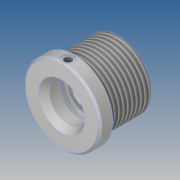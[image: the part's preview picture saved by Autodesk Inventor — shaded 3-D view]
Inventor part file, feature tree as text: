
AUTODESK INVENTOR PART (.ipt)
format: ipt  version: 2019 (Build 230136000, 136)  size: 200,704 bytes
history: native  units: mm
features: other x3, sketch x3, fillet x1, chamfer x1, extrude x1, hole x1, projected_geometry x1
ambient origin geometry x8: Origin, YZ Plane, XZ Plane, XY Plane, X Axis, Y Axis, Z Axis, Center Point
bodies: Solide1 (feature_tree)
feature tree (11):
  other  "Révolution1"
  other  "Filetage1"
  fillet  "Congé1"  Radius=17.0mm
  chamfer  "Chanfrein1"  Distance=3.0mm
  other  "Plan de construction3"
  extrude  "Extrusion4"  Depth=2.0mm
  hole  "Perçage3"  [1 undecoded]
  sketch  "Esquisse1"
  sketch  "Esquisse9"
  sketch  "Esquisse10"
  projected_geometry  "Boucle projetée3"
note: 1 required parameter value undecoded (feature->parameter linkage not recoverable at this tier; creation-order binding heuristic only, values carry confidence <= 0.55)
